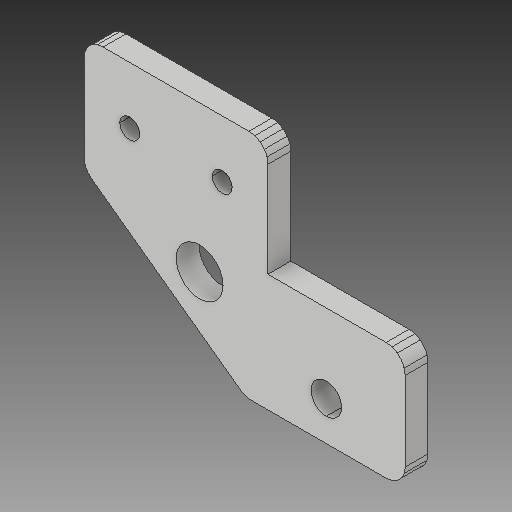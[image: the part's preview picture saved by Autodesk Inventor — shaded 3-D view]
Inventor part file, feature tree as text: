
AUTODESK INVENTOR PART (.ipt)
format: ipt  version: 2017 (Build 210142000, 142)  size: 231,936 bytes
history: native  units: mm
features: other x3, sketch x3
ambient origin geometry x8: Origin, YZ Plane, XZ Plane, XY Plane, X Axis, Y Axis, Z Axis, Center Point
bodies: Solid1 (feature_tree)
feature tree (6):
  other  "Leadscrew-rod-holder_MIR.ipt"
  other  "Solid1::Leadscrew-rod-holder_MIR.ipt"
  other  "TaggingFeature1"
  sketch  "Sketch1"  dims[d0=10.0mm]
  sketch  "Sketch2"
  sketch  "Sketch3"
